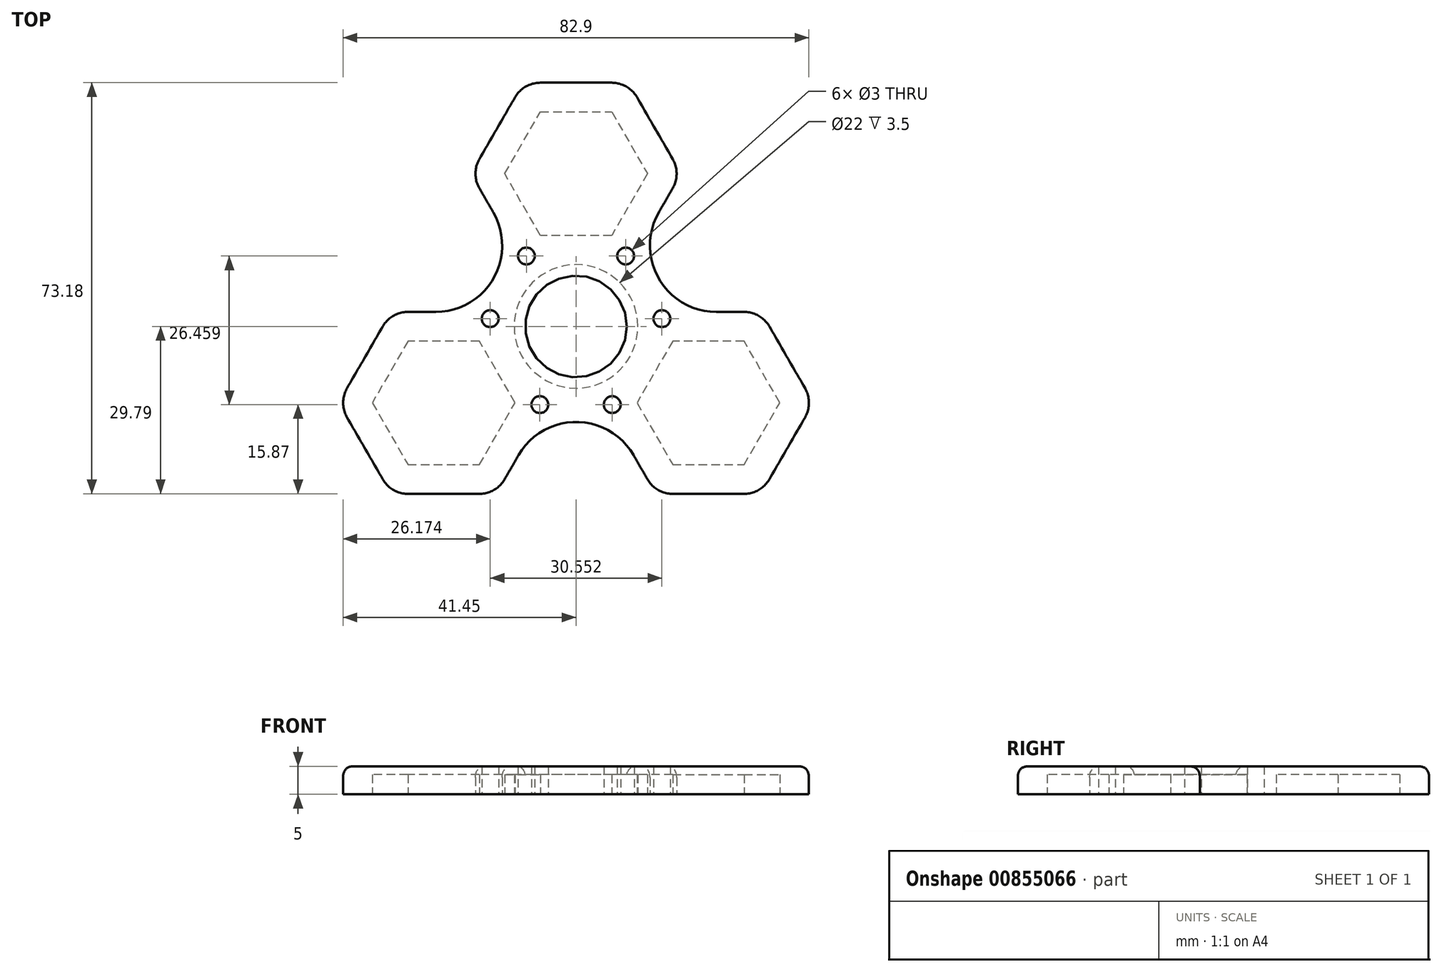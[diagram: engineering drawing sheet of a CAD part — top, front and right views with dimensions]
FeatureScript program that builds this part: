
annotation { "Feature Type Name" : "Feature", "Feature Type Description" : "" }
export const myFeature = defineFeature(function(context is Context, id is Id, definition is map)
    precondition{}
    {
        {
            var Q0;
            Q0=qCreatedBy(makeId("Top.planeOp"),FACE);
            var sketch = newSketch(context, id + "F0", { "sketchPlane" : qUnion([Q0])});
            skLineSegment(sketch, "E0.0", {"start": v(0, 27.2) * mm, "end": v(23.55, -13.6) * mm, "construction": true});
            skLineSegment(sketch, "E0.1", {"start": v(23.55, -13.6) * mm, "end": v(-23.55, -13.6) * mm, "construction": true});
            skLineSegment(sketch, "E0.2", {"start": v(-23.55, -13.6) * mm, "end": v(0, 27.2) * mm, "construction": true});
            skPoint(sketch, "E0.0.midPoint", {"position": v(11.78, 6.8) * mm});
            skLineSegment(sketch, "E1", {"start": v(-23.55, -13.6) * mm, "end": v(11.78, 6.8) * mm, "construction": true});
            skLineSegment(sketch, "E2", {"start": v(-11.78, 6.8) * mm, "end": v(23.55, -13.6) * mm, "construction": true});
            skCircle(sketch, "E3", {"center": v(0, 0) * mm, "radius": 11 * mm});
            skCircle(sketch, "E4.cCircle", {"center": v(0, 27.2) * mm, "radius": 12.7 * mm, "construction": true});
            skLineSegment(sketch, "E4.0", {"start": v(6.35, 16.2) * mm, "end": v(-6.35, 16.2) * mm});
            skLineSegment(sketch, "E4.1", {"start": v(-6.35, 16.2) * mm, "end": v(-12.7, 27.2) * mm});
            skLineSegment(sketch, "E4.2", {"start": v(-12.7, 27.2) * mm, "end": v(-6.35, 38.2) * mm});
            skLineSegment(sketch, "E4.3", {"start": v(-6.35, 38.2) * mm, "end": v(6.35, 38.2) * mm});
            skLineSegment(sketch, "E4.4", {"start": v(6.35, 38.2) * mm, "end": v(12.7, 27.2) * mm});
            skLineSegment(sketch, "E4.5", {"start": v(12.7, 27.2) * mm, "end": v(6.35, 16.2) * mm});
            skLineSegment(sketch, "E5.MirrorCS", {"start": v(10.85, -13.6) * mm, "end": v(17.2, -24.6) * mm});
            skLineSegment(sketch, "E6.MirrorCS", {"start": v(17.2, -24.6) * mm, "end": v(29.9, -24.6) * mm});
            skLineSegment(sketch, "E7.MirrorCS", {"start": v(29.9, -24.6) * mm, "end": v(36.25, -13.6) * mm});
            skLineSegment(sketch, "E8.MirrorCS", {"start": v(36.25, -13.6) * mm, "end": v(29.9, -2.6) * mm});
            skLineSegment(sketch, "E9.MirrorCS", {"start": v(29.9, -2.6) * mm, "end": v(17.2, -2.6) * mm});
            skLineSegment(sketch, "E10.MirrorCS", {"start": v(17.2, -2.6) * mm, "end": v(10.85, -13.6) * mm});
            skLineSegment(sketch, "E11.MirrorCS", {"start": v(-17.2, -2.6) * mm, "end": v(-29.9, -2.6) * mm});
            skLineSegment(sketch, "E12.MirrorCS", {"start": v(-29.9, -2.6) * mm, "end": v(-36.25, -13.6) * mm});
            skLineSegment(sketch, "E13.MirrorCS", {"start": v(-36.25, -13.6) * mm, "end": v(-29.9, -24.6) * mm});
            skLineSegment(sketch, "E14.MirrorCS", {"start": v(-29.9, -24.6) * mm, "end": v(-17.2, -24.6) * mm});
            skLineSegment(sketch, "E15.MirrorCS", {"start": v(-17.2, -24.6) * mm, "end": v(-10.85, -13.6) * mm});
            skLineSegment(sketch, "E16.MirrorCS", {"start": v(-10.85, -13.6) * mm, "end": v(-17.2, -2.6) * mm});
            skCircle(sketch, "E17.cCircle", {"center": v(0, 27.2) * mm, "radius": 18.7 * mm, "construction": true});
            skLineSegment(sketch, "E17.0", {"start": v(-9.35, 11) * mm, "end": v(-17.2, 24.6) * mm});
            skLineSegment(sketch, "E17.1", {"start": v(-17.2, 29.8) * mm, "end": v(-10.85, 40.8) * mm});
            skLineSegment(sketch, "E17.2", {"start": v(-6.35, 43.39) * mm, "end": v(6.35, 43.39) * mm});
            skLineSegment(sketch, "E17.3", {"start": v(10.85, 40.8) * mm, "end": v(17.2, 29.8) * mm});
            skLineSegment(sketch, "E17.4", {"start": v(17.2, 24.6) * mm, "end": v(9.35, 11) * mm});
            skLineSegment(sketch, "E17.5", {"start": v(9.35, 11) * mm, "end": v(-9.35, 11) * mm, "construction": true});
            skLineSegment(sketch, "E18.MirrorCS", {"start": v(14.2, 2.6) * mm, "end": v(4.85, -13.6) * mm, "construction": true});
            skLineSegment(sketch, "E19.MirrorCS", {"start": v(29.9, 2.6) * mm, "end": v(14.2, 2.6) * mm});
            skLineSegment(sketch, "E20.MirrorCS", {"start": v(40.75, -11) * mm, "end": v(34.4, 0) * mm});
            skLineSegment(sketch, "E21.MirrorCS", {"start": v(34.4, -27.2) * mm, "end": v(40.75, -16.2) * mm});
            skLineSegment(sketch, "E22.MirrorCS", {"start": v(17.2, -29.8) * mm, "end": v(29.9, -29.8) * mm});
            skLineSegment(sketch, "E23.MirrorCS", {"start": v(4.85, -13.6) * mm, "end": v(12.7, -27.2) * mm});
            skLineSegment(sketch, "E24.MirrorCS", {"start": v(-14.2, 2.6) * mm, "end": v(-29.9, 2.6) * mm});
            skLineSegment(sketch, "E25.MirrorCS", {"start": v(-34.4, 0) * mm, "end": v(-40.75, -11) * mm});
            skLineSegment(sketch, "E26.MirrorCS", {"start": v(-40.75, -16.2) * mm, "end": v(-34.4, -27.2) * mm});
            skLineSegment(sketch, "E27.MirrorCS", {"start": v(-29.9, -29.8) * mm, "end": v(-17.2, -29.8) * mm});
            skLineSegment(sketch, "E28.MirrorCS", {"start": v(-12.7, -27.2) * mm, "end": v(-4.85, -13.6) * mm});
            skLineSegment(sketch, "E29.MirrorCS", {"start": v(-4.85, -13.6) * mm, "end": v(-14.2, 2.6) * mm, "construction": true});
            skArc(sketch, "E30", {"start": v(-14.72, 20.3) * mm, "mid": v(-14.72, 8.5) * mm, "end": v(-24.95, 2.6) * mm});
            skLineSegment(sketch, "E31", {"start": v(-9.53, 5.5) * mm, "end": v(-14.72, 8.5) * mm, "construction": true});
            skLineSegment(sketch, "E32", {"start": v(-12.7, 27.2) * mm, "end": v(-18.7, 27.2) * mm, "construction": true});
            skArc(sketch, "E33.MirrorCS", {"start": v(10.22, -22.9) * mm, "mid": v(0, -17) * mm, "end": v(-10.22, -22.9) * mm});
            skArc(sketch, "E34.MirrorCS", {"start": v(24.95, 2.6) * mm, "mid": v(14.72, 8.5) * mm, "end": v(14.72, 20.3) * mm});
            skPoint(sketch, "E35.visualSharp", {"position": v(-18.7, 27.2) * mm});
            skArc(sketch, "E35.filletArc", {"start": v(-17.2, 29.8) * mm, "mid": v(-17.9, 27.2) * mm, "end": v(-17.2, 24.6) * mm});
            skPoint(sketch, "E36.visualSharp", {"position": v(-9.35, 43.39) * mm});
            skArc(sketch, "E36.filletArc", {"start": v(-6.35, 43.39) * mm, "mid": v(-8.95, 42.7) * mm, "end": v(-10.85, 40.8) * mm});
            skPoint(sketch, "E37.visualSharp", {"position": v(9.35, 43.39) * mm});
            skArc(sketch, "E37.filletArc", {"start": v(10.85, 40.8) * mm, "mid": v(8.95, 42.7) * mm, "end": v(6.35, 43.39) * mm});
            skPoint(sketch, "E38.visualSharp", {"position": v(18.7, 27.2) * mm});
            skArc(sketch, "E38.filletArc", {"start": v(17.2, 24.6) * mm, "mid": v(17.9, 27.2) * mm, "end": v(17.2, 29.8) * mm});
            skPoint(sketch, "E39.visualSharp", {"position": v(-32.9, 2.6) * mm});
            skArc(sketch, "E39.filletArc", {"start": v(-29.9, 2.6) * mm, "mid": v(-32.5, 1.9) * mm, "end": v(-34.4, 0) * mm});
            skPoint(sketch, "E40.visualSharp", {"position": v(-42.25, -13.6) * mm});
            skArc(sketch, "E40.filletArc", {"start": v(-40.75, -11) * mm, "mid": v(-41.45, -13.6) * mm, "end": v(-40.75, -16.2) * mm});
            skPoint(sketch, "E41.visualSharp", {"position": v(-32.9, -29.8) * mm});
            skArc(sketch, "E41.filletArc", {"start": v(-34.4, -27.2) * mm, "mid": v(-32.5, -29.1) * mm, "end": v(-29.9, -29.8) * mm});
            skPoint(sketch, "E42.visualSharp", {"position": v(-14.2, -29.8) * mm});
            skArc(sketch, "E42.filletArc", {"start": v(-17.2, -29.8) * mm, "mid": v(-14.6, -29.1) * mm, "end": v(-12.7, -27.2) * mm});
            skPoint(sketch, "E43.visualSharp", {"position": v(14.2, -29.8) * mm});
            skArc(sketch, "E43.filletArc", {"start": v(12.7, -27.2) * mm, "mid": v(14.6, -29.1) * mm, "end": v(17.2, -29.8) * mm});
            skPoint(sketch, "E44.visualSharp", {"position": v(32.9, -29.8) * mm});
            skArc(sketch, "E44.filletArc", {"start": v(29.9, -29.8) * mm, "mid": v(32.5, -29.1) * mm, "end": v(34.4, -27.2) * mm});
            skPoint(sketch, "E45.visualSharp", {"position": v(42.25, -13.6) * mm});
            skArc(sketch, "E45.filletArc", {"start": v(40.75, -16.2) * mm, "mid": v(41.45, -13.6) * mm, "end": v(40.75, -11) * mm});
            skPoint(sketch, "E46.visualSharp", {"position": v(32.9, 2.6) * mm});
            skArc(sketch, "E46.filletArc", {"start": v(34.4, 0) * mm, "mid": v(32.5, 1.9) * mm, "end": v(29.9, 2.6) * mm});
            skLineSegment(sketch, "E47", {"start": v(-17.2, -2.6) * mm, "end": v(-10.87, 1.7) * mm, "construction": true});
            skLineSegment(sketch, "E48", {"start": v(-10.87, 1.7) * mm, "end": v(-17.76, 5.04) * mm, "construction": true});
            skLineSegment(sketch, "E49", {"start": v(-17.76, 5.04) * mm, "end": v(-17.2, -2.6) * mm, "construction": true});
            skLineSegment(sketch, "E50", {"start": v(-14.31, 3.37) * mm, "end": v(-17.2, -2.6) * mm, "construction": true});
            skLineSegment(sketch, "E51", {"start": v(-17.48, 1.22) * mm, "end": v(-10.87, 1.7) * mm, "construction": true});
            skLineSegment(sketch, "E52", {"start": v(-17.76, 5.04) * mm, "end": v(-15.28, 1.38) * mm, "construction": true});
            skCircle(sketch, "E53", {"center": v(-15.28, 1.38) * mm, "radius": 1.5 * mm});
            skCircle(sketch, "E54.MirrorC", {"center": v(-8.83, 12.54) * mm, "radius": 1.5 * mm});
            skCircle(sketch, "E55.MirrorC", {"center": v(-6.44, -13.92) * mm, "radius": 1.5 * mm});
            skCircle(sketch, "E56.MirrorC", {"center": v(6.44, -13.92) * mm, "radius": 1.5 * mm});
            skCircle(sketch, "E57.MirrorC", {"center": v(15.28, 1.38) * mm, "radius": 1.5 * mm});
            skCircle(sketch, "E58.MirrorC", {"center": v(8.83, 12.54) * mm, "radius": 1.5 * mm});
            skLineSegment(sketch, "E59", {"start": v(0, 11) * mm, "end": v(0, 9) * mm});
            skCircle(sketch, "E60", {"center": v(0, 0) * mm, "radius": 9 * mm});
            skSolve(sketch);
        }
        {
            var Q0;
            Q0=qSketchRegion(id+"F0",true);
            var Q1;
            Q1=makeQuery(id+"F0.imprint","IMPRINT",FACE,{"disambiguationData":[TD([[makeQuery(id+"F0.imprint","IMPRINT",EDGE,{"derivedFrom":sQuery(id+"F0.wireOp",EDGE,"E11.MirrorCS")}),1.0]])]});
            var Q2;
            Q2=makeQuery(id+"F0.imprint","IMPRINT",FACE,{"disambiguationData":[TD([[makeQuery(id+"F0.imprint","IMPRINT",EDGE,{"derivedFrom":sQuery(id+"F0.wireOp",EDGE,"E4.0")}),-1.0]])]});
            var Q3;
            Q3=makeQuery(id+"F0.imprint","IMPRINT",FACE,{"disambiguationData":[TD([[makeQuery(id+"F0.imprint","IMPRINT",EDGE,{"derivedFrom":sQuery(id+"F0.wireOp",EDGE,"E5.MirrorCS")}),1.0]])]});
            var Q4;
            Q4=makeQuery(id+"F0.imprint","IMPRINT",FACE,{"disambiguationData":[TD([[makeQuery(id+"F0.imprint","IMPRINT",EDGE,{"derivedFrom":sQuery(id+"F0.wireOp",EDGE,"E3")}),1.0]])]});
            extrude(context, id + "F1", {"entities" : qUnion([Q0, Q1, Q2, Q3, Q4]), "depth" : 5 * mm, "offsetDistance" : 25.4 * mm});
        }
        {
            var Q0;
            Q0=makeQuery(id+"F1.opExtrude","CAP_EDGE",EDGE,{"disambiguationData":[OSD([sQuery(id+"F0.wireOp",EDGE,"E34.MirrorCS")])],"isStart":false});
            var Q1;
            Q1=makeQuery(id+"F1.opExtrude","CAP_EDGE",EDGE,{"disambiguationData":[OSD([sQuery(id+"F0.wireOp",EDGE,"E60")])],"isStart":false});
            fillet(context, id + "F2", {"entities" : qUnion([Q0, Q1]), "radius" : 2 * mm, "tangentPropagation" : true, "rho" : 0.5, "crossSection" : FilletCrossSection.CONIC, "allowEdgeOverflow" : false});
        }
        {
            var Q0;
            Q0=makeQuery(id+"F0.imprint","IMPRINT",FACE,{"disambiguationData":[TD([[makeQuery(id+"F0.imprint","IMPRINT",EDGE,{"derivedFrom":sQuery(id+"F0.wireOp",EDGE,"E5.MirrorCS")}),1.0]])]});
            var Q1;
            Q1=makeQuery(id+"F0.imprint","IMPRINT",FACE,{"disambiguationData":[TD([[makeQuery(id+"F0.imprint","IMPRINT",EDGE,{"derivedFrom":sQuery(id+"F0.wireOp",EDGE,"E11.MirrorCS")}),1.0]])]});
            var Q2;
            Q2=makeQuery(id+"F0.imprint","IMPRINT",FACE,{"disambiguationData":[TD([[makeQuery(id+"F0.imprint","IMPRINT",EDGE,{"derivedFrom":sQuery(id+"F0.wireOp",EDGE,"E4.0")}),-1.0]])]});
            var Q3;
            Q3=makeQuery(id+"F0.imprint","IMPRINT",FACE,{"disambiguationData":[TD([[makeQuery(id+"F0.imprint","IMPRINT",EDGE,{"derivedFrom":sQuery(id+"F0.wireOp",EDGE,"E3")}),1.0]])]});
            extrude(context, id + "F3", {"entities" : qUnion([Q0, Q1, Q2, Q3]), "operationType" : NewBodyOperationType.REMOVE, "depth" : 3.5 * mm, "offsetDistance" : 25.4 * mm});
        }
    });
